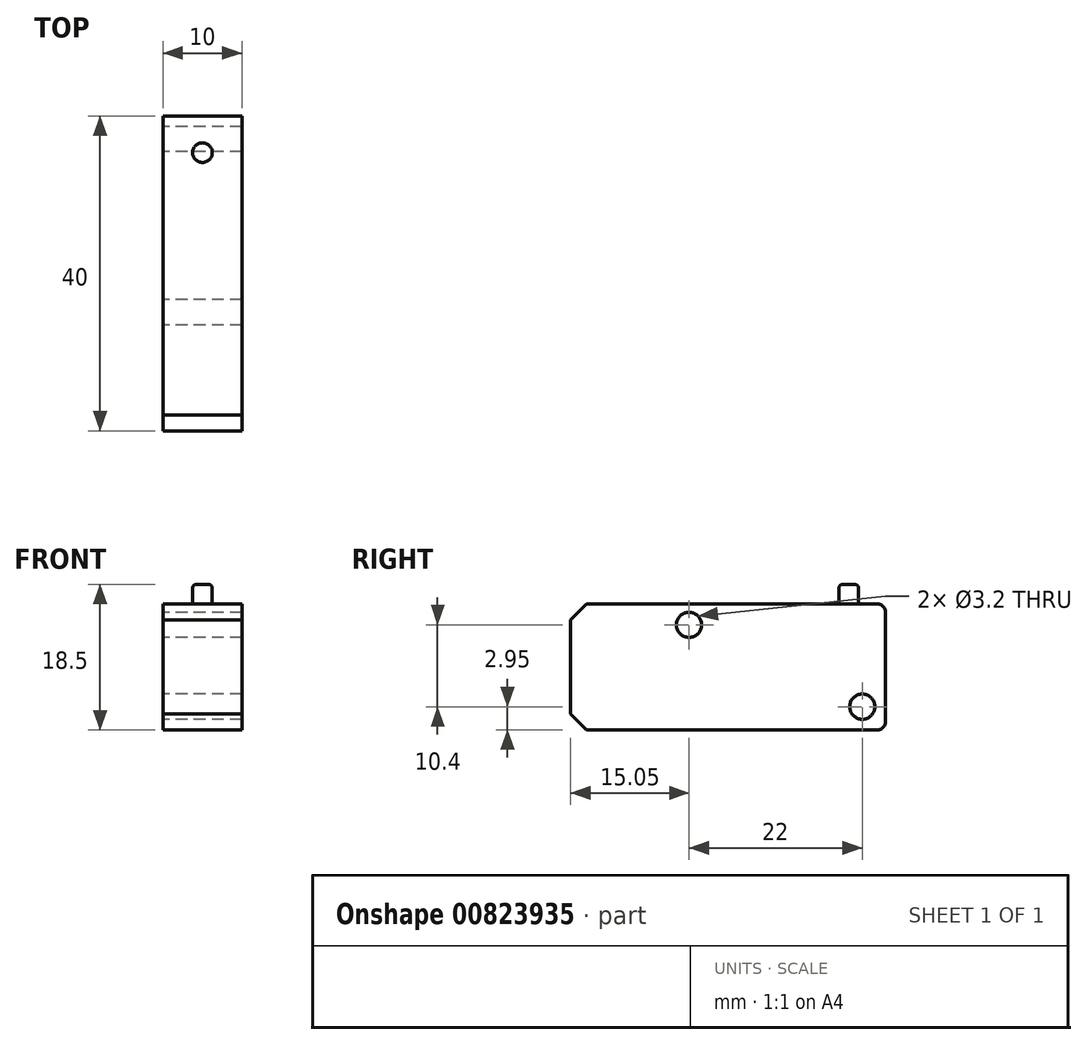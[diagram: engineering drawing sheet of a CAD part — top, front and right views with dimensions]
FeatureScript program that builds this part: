
annotation { "Feature Type Name" : "Feature", "Feature Type Description" : "" }
export const myFeature = defineFeature(function(context is Context, id is Id, definition is map)
    precondition{}
    {
        {
            var Q0;
            Q0=qCreatedBy(makeId("Top.planeOp"),FACE);
            var sketch = newSketch(context, id + "F0", { "sketchPlane" : qUnion([Q0])});
            skLineSegment(sketch, "E0.bottom", {"start": v(5, -20) * mm, "end": v(-5, -20) * mm});
            skLineSegment(sketch, "E0.top", {"start": v(5, 20) * mm, "end": v(-5, 20) * mm});
            skLineSegment(sketch, "E0.left", {"start": v(5, -20) * mm, "end": v(5, 20) * mm});
            skLineSegment(sketch, "E0.right", {"start": v(-5, -20) * mm, "end": v(-5, 20) * mm});
            skPoint(sketch, "E0.middle", {"position": v(0, 0) * mm});
            skSolve(sketch);
        }
        {
            var Q0;
            Q0=makeQuery(id+"F0.imprint","IMPRINT",FACE,{"disambiguationData":[TD([[makeQuery(id+"F0.imprint","IMPRINT",EDGE,{"derivedFrom":sQuery(id+"F0.wireOp",EDGE,"E0.bottom")}),-1.0]])]});
            extrude(context, id + "F1", {"entities" : qUnion([Q0]), "depth" : 16 * mm, "offsetDistance" : 25 * mm});
        }
        {
            var Q0;
            Q0=qCreatedBy(makeId("Top.planeOp"),FACE);
            var sketch = newSketch(context, id + "F2", { "sketchPlane" : qUnion([Q0])});
            skLineSegment(sketch, "E1.bottom", {"start": v(5005, -20) * mm, "end": v(-5005, -20) * mm});
            skLineSegment(sketch, "E1.top", {"start": v(5005, 20) * mm, "end": v(-5005, 20) * mm});
            skLineSegment(sketch, "E1.left", {"start": v(5005, -20) * mm, "end": v(5005, 20) * mm});
            skLineSegment(sketch, "E1.right", {"start": v(-5005, -20) * mm, "end": v(-5005, 20) * mm});
            skPoint(sketch, "E1.middle", {"position": v(0, 0) * mm});
            skSolve(sketch);
        }
        {
            var Q0;
            Q0=makeQuery(id+"F1.opExtrude","CAP_FACE",FACE,{"disambiguationData":[OSD([sQuery(id+"F0.wireOp",EDGE,"E0.bottom"),sQuery(id+"F0.wireOp",EDGE,"E0.top"),sQuery(id+"F0.wireOp",EDGE,"E0.left"),sQuery(id+"F0.wireOp",EDGE,"E0.right")])],"isStart":false});
            var sketch = newSketch(context, id + "F3", { "sketchPlane" : qUnion([Q0])});
            skCircle(sketch, "E2", {"center": v(0, 15.33) * mm, "radius": 1.25 * mm});
            skSolve(sketch);
        }
        {
            var Q0;
            Q0=makeQuery(id+"F3.imprint","IMPRINT",FACE,{"disambiguationData":[TD([[makeQuery(id+"F3.imprint","IMPRINT",EDGE,{"derivedFrom":sQuery(id+"F3.wireOp",EDGE,"E2")}),1.0]])]});
            extrude(context, id + "F4", {"entities" : qUnion([Q0]), "operationType" : NewBodyOperationType.ADD, "depth" : 2.5 * mm, "offsetDistance" : 25 * mm});
        }
        {
            var Q0;
            Q0=makeQuery(id+"F4.opExtrude","CAP_EDGE",EDGE,{"disambiguationData":[OSD([sQuery(id+"F3.wireOp",EDGE,"E2")])],"isStart":false});
            fillet(context, id + "F5", {"entities" : qUnion([Q0]), "radius" : 0.5 * mm, "tangentPropagation" : true, "allowEdgeOverflow" : false});
        }
        {
            var Q0;
            Q0=makeQuery(id+"F1.opExtrude","CAP_EDGE",EDGE,{"disambiguationData":[OSD([sQuery(id+"F0.wireOp",EDGE,"E0.top")])],"isStart":false});
            var Q1;
            Q1=makeQuery(id+"F1.opExtrude","CAP_EDGE",EDGE,{"disambiguationData":[OSD([sQuery(id+"F0.wireOp",EDGE,"E0.top")])],"isStart":true});
            fillet(context, id + "F6", {"entities" : qUnion([Q0, Q1]), "radius" : 1 * mm, "tangentPropagation" : true, "allowEdgeOverflow" : false});
        }
        {
            var Q0;
            Q0=makeQuery(id+"F1.opExtrude","CAP_EDGE",EDGE,{"disambiguationData":[OSD([sQuery(id+"F0.wireOp",EDGE,"E0.bottom")])],"isStart":true});
            var Q1;
            Q1=makeQuery(id+"F1.opExtrude","CAP_EDGE",EDGE,{"disambiguationData":[OSD([sQuery(id+"F0.wireOp",EDGE,"E0.bottom")])],"isStart":false});
            chamfer(context, id + "F7", {"entities" : qUnion([Q0, Q1]), "width" : 2 * mm, "tangentPropagation" : true});
        }
        {
            var Q0;
            Q0=makeQuery(id+"F1.opExtrude","SWEPT_FACE",FACE,{"disambiguationData":[OSD([sQuery(id+"F0.wireOp",EDGE,"E0.right")])]});
            var sketch = newSketch(context, id + "F8", { "sketchPlane" : qUnion([Q0])});
            skCircle(sketch, "E3", {"center": v(-17.05, 2.95) * mm, "radius": 1.6 * mm});
            skCircle(sketch, "E4", {"center": v(4.95, 13.35) * mm, "radius": 1.6 * mm});
            skSolve(sketch);
        }
        {
            var Q0;
            Q0=makeQuery(id+"F8.imprint","IMPRINT",FACE,{"disambiguationData":[TD([[makeQuery(id+"F8.imprint","IMPRINT",EDGE,{"derivedFrom":sQuery(id+"F8.wireOp",EDGE,"E3")}),1.0]])]});
            var Q1;
            Q1=makeQuery(id+"F8.imprint","IMPRINT",FACE,{"disambiguationData":[TD([[makeQuery(id+"F8.imprint","IMPRINT",EDGE,{"derivedFrom":sQuery(id+"F8.wireOp",EDGE,"E4")}),1.0]])]});
            extrude(context, id + "F9", {"entities" : qUnion([Q0, Q1]), "operationType" : NewBodyOperationType.REMOVE, "endBound" : BoundingType.THROUGH_ALL, "oppositeDirection" : true, "depth" : 25 * mm, "offsetDistance" : 25 * mm});
        }
    });
